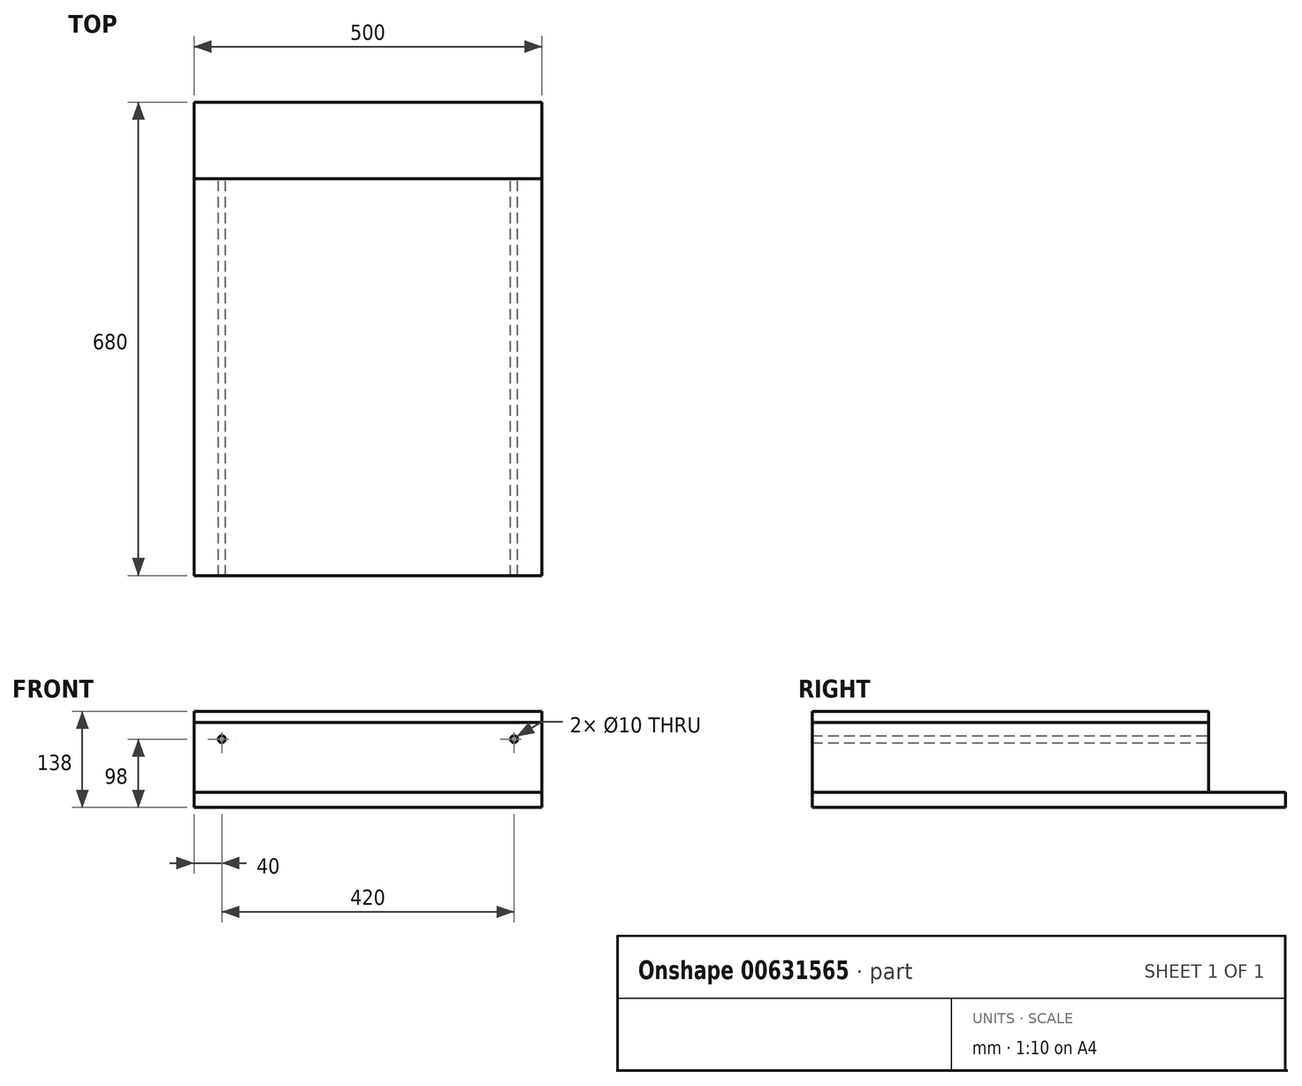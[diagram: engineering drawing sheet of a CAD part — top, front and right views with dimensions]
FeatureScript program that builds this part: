
annotation { "Feature Type Name" : "Feature", "Feature Type Description" : "" }
export const myFeature = defineFeature(function(context is Context, id is Id, definition is map)
    precondition{}
    {
        {
            var Q0;
            Q0=qCreatedBy(makeId("Top.planeOp"),FACE);
            var sketch = newSketch(context, id + "F0", { "sketchPlane" : qUnion([Q0])});
            skLineSegment(sketch, "E0.bottom", {"start": v(250, 285) * mm, "end": v(-250, 285) * mm});
            skLineSegment(sketch, "E0.top", {"start": v(250, -285) * mm, "end": v(-250, -285) * mm});
            skLineSegment(sketch, "E0.left", {"start": v(250, 285) * mm, "end": v(250, -285) * mm});
            skLineSegment(sketch, "E0.right", {"start": v(-250, 285) * mm, "end": v(-250, -285) * mm});
            skPoint(sketch, "E0.middle", {"position": v(0, 0) * mm});
            skSolve(sketch);
        }
        {
            var Q0;
            Q0 = qSketchRegion(id + "F0", true);
            extrude(context, id + "F1", {"entities" : qUnion([Q0]), "depth" : 16 * mm, "offsetDistance" : 25 * mm});
        }
        {
            var Q0;
            Q0 = qSketchRegion(id + "F0", true);
            var Q1;
            Q1=sQuery(id+"F0.wireOp",EDGE,"E0.top");
            var Q2;
            Q2=sQuery(id+"F0.wireOp",EDGE,"E0.right");
            var Q3;
            Q3=sQuery(id+"F0.wireOp",EDGE,"E0.left");
            var Q4;
            Q4=sQuery(id+"F0.wireOp",EDGE,"E0.bottom");
            extrude(context, id + "F2", {"entities" : qUnion([Q0]), "surfaceEntities" : qUnion([Q1, Q2, Q3, Q4]), "oppositeDirection" : true, "depth" : 100 * mm, "offsetDistance" : 25 * mm});
        }
        {
            var Q0;
            Q0=makeQuery(id+"F2.opExtrude","CAP_FACE",FACE,{"disambiguationData":[OSD([sQuery(id+"F0.wireOp",EDGE,"E0.bottom"),sQuery(id+"F0.wireOp",EDGE,"E0.top"),sQuery(id+"F0.wireOp",EDGE,"E0.left"),sQuery(id+"F0.wireOp",EDGE,"E0.right")])],"isStart":false});
            var sketch = newSketch(context, id + "F3", { "sketchPlane" : qUnion([Q0])});
            skLineSegment(sketch, "E1.bottom", {"start": v(250, 285) * mm, "end": v(-250, 285) * mm});
            skLineSegment(sketch, "E1.top", {"start": v(250, -395) * mm, "end": v(-250, -395) * mm});
            skLineSegment(sketch, "E1.left", {"start": v(250, 285) * mm, "end": v(250, -395) * mm});
            skLineSegment(sketch, "E1.right", {"start": v(-250, 285) * mm, "end": v(-250, -395) * mm});
            skSolve(sketch);
        }
        {
            var Q0;
            Q0 = qSketchRegion(id + "F3", true);
            extrude(context, id + "F4", {"entities" : qUnion([Q0]), "depth" : 22 * mm, "offsetDistance" : 25 * mm});
        }
        {
            var Q0;
            Q0=makeQuery(id+"F2.opExtrude","SWEPT_FACE",FACE,{"disambiguationData":[OSD([sQuery(id+"F0.wireOp",EDGE,"E0.bottom")])]});
            var sketch = newSketch(context, id + "F5", { "sketchPlane" : qUnion([Q0])});
            skLineSegment(sketch, "E2", {"start": v(0, 0) * mm, "end": v(0, -100) * mm, "construction": true});
            skCircle(sketch, "E3", {"center": v(-210, -24) * mm, "radius": 5 * mm});
            skCircle(sketch, "E4", {"center": v(210, -24) * mm, "radius": 5 * mm});
            skLineSegment(sketch, "E5", {"start": v(-250, -24) * mm, "end": v(250, -24) * mm, "construction": true});
            skSolve(sketch);
        }
        {
            var Q0;
            Q0 = qSketchRegion(id + "F5", true);
            var Q1;
            Q1=makeQuery(id+"F2.opExtrude","SWEPT_FACE",FACE,{"disambiguationData":[OSD([sQuery(id+"F0.wireOp",EDGE,"E0.top")])]});
            extrude(context, id + "F6", {"entities" : qUnion([Q0]), "operationType" : NewBodyOperationType.REMOVE, "endBound" : BoundingType.UP_TO_SURFACE, "oppositeDirection" : true, "depth" : 25 * mm, "endBoundEntityFace" : qUnion([Q1]), "offsetDistance" : 25 * mm});
        }
    });
